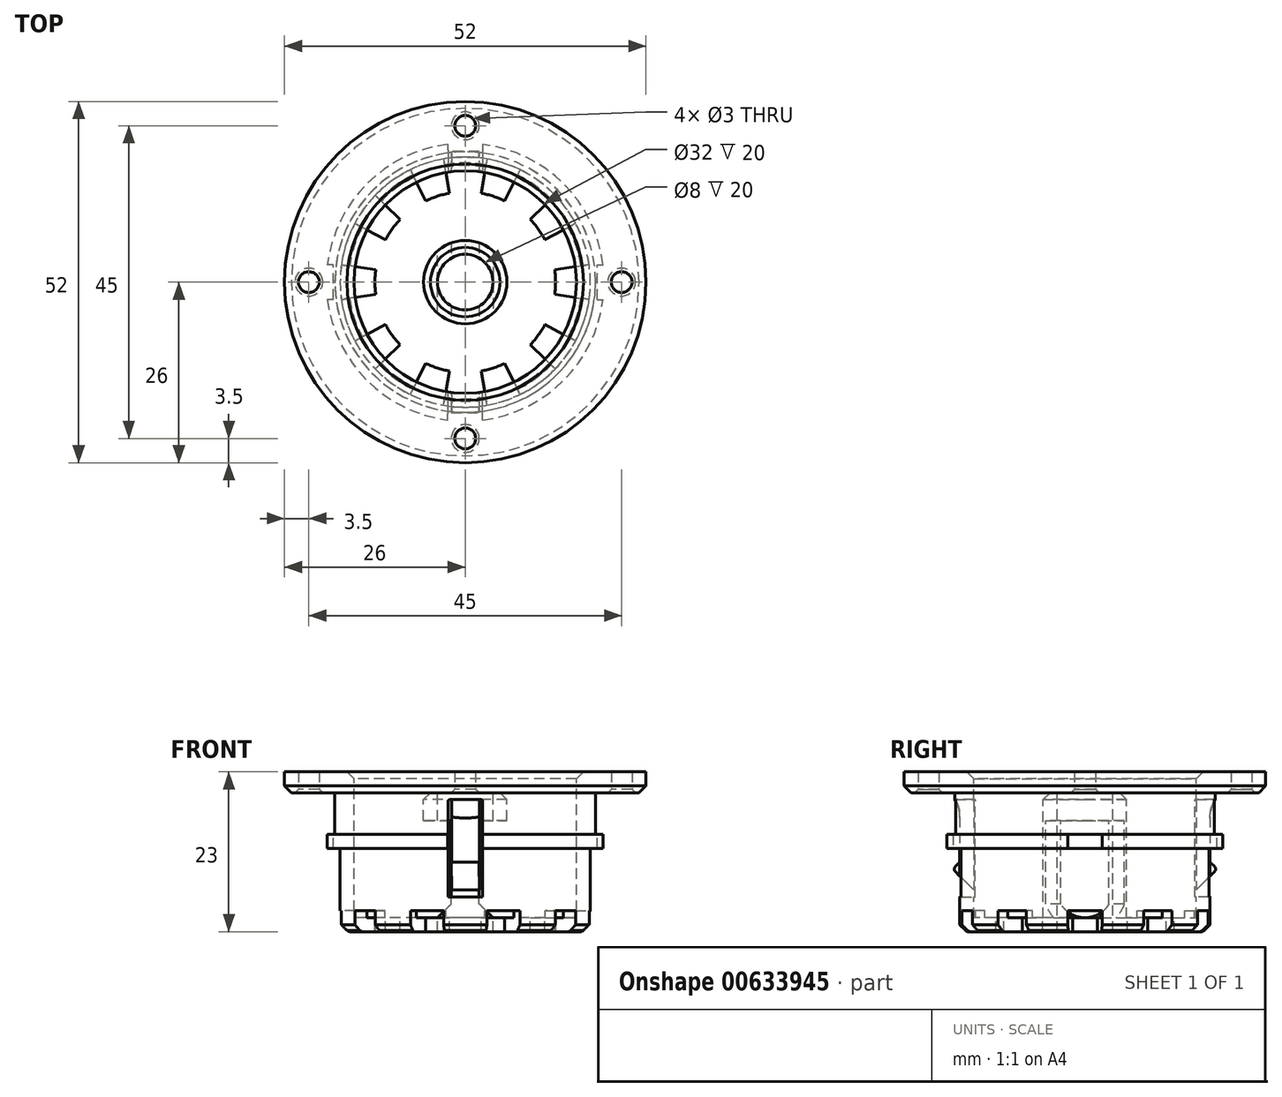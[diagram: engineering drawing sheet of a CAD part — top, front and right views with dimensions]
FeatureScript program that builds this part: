
annotation { "Feature Type Name" : "Feature", "Feature Type Description" : "" }
export const myFeature = defineFeature(function(context is Context, id is Id, definition is map)
    precondition{}
    {
        {
            var Q0;
            Q0=qCreatedBy(makeId("Top.planeOp"),FACE);
            var sketch = newSketch(context, id + "F0", { "sketchPlane" : qUnion([Q0])});
            skCircle(sketch, "E0", {"center": v(0, 0) * mm, "radius": 18 * mm});
            skSolve(sketch);
        }
        {
            var Q0;
            Q0=qCreatedBy(makeId("Top.planeOp"),FACE);
            var sketch = newSketch(context, id + "F1", { "sketchPlane" : qUnion([Q0])});
            skCircle(sketch, "E1", {"center": v(0, 0) * mm, "radius": 18.75 * mm});
            skSolve(sketch);
        }
        {
            var Q0;
            Q0=qCreatedBy(makeId("Top.planeOp"),FACE);
            var sketch = newSketch(context, id + "F2", { "sketchPlane" : qUnion([Q0])});
            skCircle(sketch, "E2", {"center": v(0, 0) * mm, "radius": 20 * mm});
            skLineSegment(sketch, "E3.bottom", {"start": v(19, -2.5) * mm, "end": v(21, -2.5) * mm});
            skLineSegment(sketch, "E3.top", {"start": v(19, 2.5) * mm, "end": v(21, 2.5) * mm});
            skLineSegment(sketch, "E3.left", {"start": v(19, -2.5) * mm, "end": v(19, 2.5) * mm});
            skLineSegment(sketch, "E3.right", {"start": v(21, -2.5) * mm, "end": v(21, 2.5) * mm});
            skPoint(sketch, "E3.middle", {"position": v(20, 0) * mm});
            skLineSegment(sketch, "E4.MirrorCS", {"start": v(-19, -2.5) * mm, "end": v(-21, -2.5) * mm});
            skLineSegment(sketch, "E5.MirrorCS", {"start": v(-21, -2.5) * mm, "end": v(-21, 2.5) * mm});
            skLineSegment(sketch, "E6.MirrorCS", {"start": v(-19, -2.5) * mm, "end": v(-19, 2.5) * mm});
            skLineSegment(sketch, "E7.MirrorCS", {"start": v(-19, 2.5) * mm, "end": v(-21, 2.5) * mm});
            skPoint(sketch, "E8.MirrorP", {"position": v(-20, 0) * mm});
            skLineSegment(sketch, "E9.bottom", {"start": v(2.5, -19) * mm, "end": v(-2.5, -19) * mm});
            skLineSegment(sketch, "E9.top", {"start": v(2.5, -21) * mm, "end": v(-2.5, -21) * mm});
            skLineSegment(sketch, "E9.left", {"start": v(2.5, -21) * mm, "end": v(2.5, -19) * mm});
            skLineSegment(sketch, "E9.right", {"start": v(-2.5, -21) * mm, "end": v(-2.5, -19) * mm});
            skPoint(sketch, "E9.middle", {"position": v(0, -20) * mm});
            skLineSegment(sketch, "E10.MirrorCS", {"start": v(2.5, 21) * mm, "end": v(2.5, 19) * mm});
            skLineSegment(sketch, "E11.MirrorCS", {"start": v(2.5, 21) * mm, "end": v(-2.5, 21) * mm});
            skLineSegment(sketch, "E12.MirrorCS", {"start": v(2.5, 19) * mm, "end": v(-2.5, 19) * mm});
            skLineSegment(sketch, "E13.MirrorCS", {"start": v(-2.5, 21) * mm, "end": v(-2.5, 19) * mm});
            skSolve(sketch);
        }
        {
            var Q0;
            Q0 = qSketchRegion(id + "F0", true);
            extrude(context, id + "F3", {"entities" : qUnion([Q0]), "oppositeDirection" : true, "depth" : 20 * mm, "offsetDistance" : 25 * mm});
        }
        {
            var Q0;
            Q0 = qSketchRegion(id + "F1", true);
            extrude(context, id + "F4", {"entities" : qUnion([Q0]), "operationType" : NewBodyOperationType.ADD, "oppositeDirection" : true, "depth" : 6 * mm, "offsetDistance" : 25 * mm});
        }
        {
            var Q0;
            {var subQ13=sQuery(id+"F2.wireOp",EDGE,"E3.left");Q0=makeQuery(id+"F2.imprint","IMPRINT",FACE,{"disambiguationData":[TD([[makeQuery(id+"F2.imprint","IMPRINT",EDGE,{"derivedFrom":subQ13}),1.0]])]});}
            extrude(context, id + "F5", {"entities" : qUnion([Q0]), "operationType" : NewBodyOperationType.ADD, "oppositeDirection" : true, "depth" : 8 * mm, "offsetDistance" : 25 * mm, "hasSecondDirection" : true, "secondDirectionOppositeDirection" : true, "secondDirectionDepth" : 6 * mm});
        }
        {
            var Q0;
            Q0=qCreatedBy(makeId("Top.planeOp"),FACE);
            var sketch = newSketch(context, id + "F6", { "sketchPlane" : qUnion([Q0])});
            skCircle(sketch, "E14", {"center": v(0, 0) * mm, "radius": 4 * mm});
            skSolve(sketch);
        }
        {
            var Q0;
            Q0 = qSketchRegion(id + "F6", true);
            extrude(context, id + "F7", {"entities" : qUnion([Q0]), "operationType" : NewBodyOperationType.REMOVE, "oppositeDirection" : true, "depth" : 20 * mm, "offsetDistance" : 25 * mm});
        }
        {
            var Q0;
            Q0=qCreatedBy(makeId("Top.planeOp"),FACE);
            var sketch = newSketch(context, id + "F8", { "sketchPlane" : qUnion([Q0])});
            skCircle(sketch, "E15", {"center": v(0, 0) * mm, "radius": 16 * mm});
            skCircle(sketch, "E16", {"center": v(0, 0) * mm, "radius": 6 * mm});
            skSolve(sketch);
        }
        {
            var Q0;
            Q0 = qSketchRegion(id + "F8", true);
            extrude(context, id + "F9", {"entities" : qUnion([Q0]), "operationType" : NewBodyOperationType.REMOVE, "oppositeDirection" : true, "depth" : 18 * mm, "offsetDistance" : 25 * mm});
        }
        {
            var Q0;
            Q0=qCreatedBy(makeId("Top.planeOp"),FACE);
            var sketch = newSketch(context, id + "F10", { "sketchPlane" : qUnion([Q0])});
            skLineSegment(sketch, "E17.bottom", {"start": v(6, 6) * mm, "end": v(2, 6) * mm});
            skLineSegment(sketch, "E17.top", {"start": v(6, -6) * mm, "end": v(2, -6) * mm});
            skLineSegment(sketch, "E17.left", {"start": v(6, 6) * mm, "end": v(6, -6) * mm});
            skLineSegment(sketch, "E17.right", {"start": v(2, 6) * mm, "end": v(2, -6) * mm});
            skPoint(sketch, "E17.middle", {"position": v(4, 0) * mm});
            skPoint(sketch, "E18.MirrorP", {"position": v(-4, 0) * mm});
            skLineSegment(sketch, "E19.MirrorCS", {"start": v(-6, 6) * mm, "end": v(-2, 6) * mm});
            skLineSegment(sketch, "E20.MirrorCS", {"start": v(-6, 6) * mm, "end": v(-6, -6) * mm});
            skLineSegment(sketch, "E21.MirrorCS", {"start": v(-6, -6) * mm, "end": v(-2, -6) * mm});
            skLineSegment(sketch, "E22.MirrorCS", {"start": v(-2, 6) * mm, "end": v(-2, -6) * mm});
            skSolve(sketch);
        }
        {
            var Q0;
            Q0 = qSketchRegion(id + "F10", true);
            extrude(context, id + "F11", {"entities" : qUnion([Q0]), "operationType" : NewBodyOperationType.REMOVE, "oppositeDirection" : true, "depth" : 18 * mm, "offsetDistance" : 25 * mm, "hasSecondDirection" : true, "secondDirectionOppositeDirection" : true, "secondDirectionDepth" : 4 * mm});
        }
        {
            var Q0;
            Q0=qCreatedBy(makeId("Top.planeOp"),FACE);
            var sketch = newSketch(context, id + "F12", { "sketchPlane" : qUnion([Q0])});
            skCircle(sketch, "E23", {"center": v(0, 0) * mm, "radius": 16 * mm});
            skCircle(sketch, "E24", {"center": v(0, 0) * mm, "radius": 26 * mm});
            skCircle(sketch, "E25", {"center": v(0, 22.5) * mm, "radius": 1.5 * mm});
            skCircle(sketch, "E26.MirrorC", {"center": v(0, -22.5) * mm, "radius": 1.5 * mm});
            skCircle(sketch, "E27", {"center": v(-22.5, 0) * mm, "radius": 1.5 * mm});
            skCircle(sketch, "E28.MirrorC", {"center": v(22.5, 0) * mm, "radius": 1.5 * mm});
            skSolve(sketch);
        }
        {
            var Q0;
            Q0 = qSketchRegion(id + "F12", true);
            extrude(context, id + "F13", {"entities" : qUnion([Q0]), "operationType" : NewBodyOperationType.ADD, "depth" : 3 * mm, "offsetDistance" : 25 * mm});
        }
        {
            var Q0;
            Q0=makeQuery(id+"F11.boolean.opBoolean","COPY",EDGE,{"disambiguationData":[OD(1.0)],"derivedFrom":makeQuery(id+"F11.opExtrude","CAP_EDGE",EDGE,{"disambiguationData":[OSD([sQuery(id+"F10.wireOp",EDGE,"E17.right")])],"isStart":false})});
            var Q1;
            Q1=makeQuery(id+"F11.boolean.opBoolean","COPY",EDGE,{"disambiguationData":[OD(1.0)],"derivedFrom":makeQuery(id+"F11.opExtrude","CAP_EDGE",EDGE,{"disambiguationData":[OSD([sQuery(id+"F10.wireOp",EDGE,"E22.MirrorCS")])],"isStart":false})});
            var Q2;
            Q2=makeQuery(id+"F11.boolean.opBoolean","COPY",EDGE,{"disambiguationData":[OD(0.0)],"derivedFrom":makeQuery(id+"F11.opExtrude","CAP_EDGE",EDGE,{"disambiguationData":[OSD([sQuery(id+"F10.wireOp",EDGE,"E22.MirrorCS")])],"isStart":false})});
            var Q3;
            Q3=makeQuery(id+"F11.boolean.opBoolean","COPY",EDGE,{"disambiguationData":[OD(0.0)],"derivedFrom":makeQuery(id+"F11.opExtrude","CAP_EDGE",EDGE,{"disambiguationData":[OSD([sQuery(id+"F10.wireOp",EDGE,"E17.right")])],"isStart":false})});
            chamfer(context, id + "F14", {"entities" : qUnion([Q0, Q1, Q2, Q3]), "width" : 2 * mm, "tangentPropagation" : true});
        }
        {
            var Q0;
            Q0=makeQuery(id+"F13.opExtrude","CAP_EDGE",EDGE,{"disambiguationData":[OSD([sQuery(id+"F12.wireOp",EDGE,"E23")])],"isStart":false});
            chamfer(context, id + "F15", {"entities" : qUnion([Q0]), "width" : 1 * mm, "tangentPropagation" : true});
        }
        {
            var Q0;
            Q0=makeQuery(id+"F13.opExtrude","CAP_EDGE",EDGE,{"disambiguationData":[OSD([sQuery(id+"F12.wireOp",EDGE,"E26.MirrorC")])],"isStart":true});
            var Q1;
            Q1=makeQuery(id+"F13.opExtrude","CAP_EDGE",EDGE,{"disambiguationData":[OSD([sQuery(id+"F12.wireOp",EDGE,"E28.MirrorC")])],"isStart":true});
            var Q2;
            Q2=makeQuery(id+"F13.opExtrude","CAP_EDGE",EDGE,{"disambiguationData":[OSD([sQuery(id+"F12.wireOp",EDGE,"E25")])],"isStart":true});
            var Q3;
            Q3=makeQuery(id+"F13.opExtrude","CAP_EDGE",EDGE,{"disambiguationData":[OSD([sQuery(id+"F12.wireOp",EDGE,"E27")])],"isStart":true});
            chamfer(context, id + "F16", {"entities" : qUnion([Q0, Q1, Q2, Q3]), "width" : 0.5 * mm, "tangentPropagation" : true});
        }
        {
            var Q0;
            Q0=makeQuery(id+"F3.opExtrude","CAP_EDGE",EDGE,{"disambiguationData":[OSD([sQuery(id+"F0.wireOp",EDGE,"E0")])],"isStart":false});
            var Q1;
            Q1=makeQuery(id+"F13.opExtrude","CAP_EDGE",EDGE,{"disambiguationData":[OSD([sQuery(id+"F12.wireOp",EDGE,"E24")])],"isStart":true});
            var Q2;
            Q2=makeQuery(id+"F7.boolean.opBoolean","COPY",EDGE,{"derivedFrom":makeQuery(id+"F7.opExtrude","CAP_EDGE",EDGE,{"disambiguationData":[OSD([sQuery(id+"F6.wireOp",EDGE,"E14")])],"isStart":false})});
            var Q3;
            Q3=makeQuery(id+"F9.boolean.opBoolean","COPY",EDGE,{"derivedFrom":makeQuery(id+"F9.opExtrude","CAP_EDGE",EDGE,{"disambiguationData":[OSD([sQuery(id+"F8.wireOp",EDGE,"E16")])],"isStart":true})});
            chamfer(context, id + "F17", {"entities" : qUnion([Q0, Q1, Q2, Q3]), "width" : 1 * mm, "tangentPropagation" : true});
        }
        {
            var Q0;
            Q0=qCreatedBy(makeId("Top.planeOp"),FACE);
            var sketch = newSketch(context, id + "F18", { "sketchPlane" : qUnion([Q0])});
            skLineSegment(sketch, "E29", {"start": v(12.88, 1.8) * mm, "end": v(17.83, 2.5) * mm});
            skLineSegment(sketch, "E30", {"start": v(12.88, -1.8) * mm, "end": v(17.83, -2.5) * mm});
            skArc(sketch, "E31", {"start": v(12.88, -1.8) * mm, "mid": v(13, 0) * mm, "end": v(12.88, 1.8) * mm});
            skArc(sketch, "E32", {"start": v(17.83, -2.5) * mm, "mid": v(18, 0) * mm, "end": v(17.83, 2.5) * mm});
            skArc(sketch, "E33.1.0", {"start": v(11.47, 6.11) * mm, "mid": v(10.52, 7.64) * mm, "end": v(9.36, 9.02) * mm});
            skLineSegment(sketch, "E33.1.1", {"start": v(11.47, 6.11) * mm, "end": v(15.9, 8.46) * mm});
            skArc(sketch, "E33.1.2", {"start": v(15.9, 8.46) * mm, "mid": v(14.56, 10.58) * mm, "end": v(12.95, 12.5) * mm});
            skLineSegment(sketch, "E33.1.3", {"start": v(9.36, 9.02) * mm, "end": v(12.95, 12.5) * mm});
            skArc(sketch, "E33.2.0", {"start": v(5.69, 11.69) * mm, "mid": v(4.02, 12.36) * mm, "end": v(2.27, 12.8) * mm});
            skLineSegment(sketch, "E33.2.1", {"start": v(5.69, 11.69) * mm, "end": v(7.89, 16.18) * mm});
            skArc(sketch, "E33.2.2", {"start": v(7.89, 16.18) * mm, "mid": v(5.56, 17.12) * mm, "end": v(3.13, 17.73) * mm});
            skLineSegment(sketch, "E33.2.3", {"start": v(2.27, 12.8) * mm, "end": v(3.13, 17.73) * mm});
            skArc(sketch, "E33.3.0", {"start": v(-2.27, 12.8) * mm, "mid": v(-4.02, 12.36) * mm, "end": v(-5.69, 11.69) * mm});
            skLineSegment(sketch, "E33.3.1", {"start": v(-2.27, 12.8) * mm, "end": v(-3.13, 17.73) * mm});
            skArc(sketch, "E33.3.2", {"start": v(-3.13, 17.73) * mm, "mid": v(-5.56, 17.12) * mm, "end": v(-7.89, 16.18) * mm});
            skLineSegment(sketch, "E33.3.3", {"start": v(-5.69, 11.69) * mm, "end": v(-7.89, 16.18) * mm});
            skArc(sketch, "E33.4.0", {"start": v(-9.36, 9.02) * mm, "mid": v(-10.52, 7.64) * mm, "end": v(-11.47, 6.11) * mm});
            skLineSegment(sketch, "E33.4.1", {"start": v(-9.36, 9.02) * mm, "end": v(-12.95, 12.5) * mm});
            skArc(sketch, "E33.4.2", {"start": v(-12.95, 12.5) * mm, "mid": v(-14.56, 10.58) * mm, "end": v(-15.9, 8.46) * mm});
            skLineSegment(sketch, "E33.4.3", {"start": v(-11.47, 6.11) * mm, "end": v(-15.9, 8.46) * mm});
            skArc(sketch, "E33.5.0", {"start": v(-12.88, 1.8) * mm, "mid": v(-13, 0) * mm, "end": v(-12.88, -1.8) * mm});
            skLineSegment(sketch, "E33.5.1", {"start": v(-12.88, 1.8) * mm, "end": v(-17.83, 2.5) * mm});
            skArc(sketch, "E33.5.2", {"start": v(-17.83, 2.5) * mm, "mid": v(-18, 0) * mm, "end": v(-17.83, -2.5) * mm});
            skLineSegment(sketch, "E33.5.3", {"start": v(-12.88, -1.8) * mm, "end": v(-17.83, -2.5) * mm});
            skArc(sketch, "E33.6.0", {"start": v(-11.47, -6.11) * mm, "mid": v(-10.52, -7.64) * mm, "end": v(-9.36, -9.02) * mm});
            skLineSegment(sketch, "E33.6.1", {"start": v(-11.47, -6.11) * mm, "end": v(-15.9, -8.46) * mm});
            skArc(sketch, "E33.6.2", {"start": v(-15.9, -8.46) * mm, "mid": v(-14.56, -10.58) * mm, "end": v(-12.95, -12.5) * mm});
            skLineSegment(sketch, "E33.6.3", {"start": v(-9.36, -9.02) * mm, "end": v(-12.95, -12.5) * mm});
            skArc(sketch, "E33.7.0", {"start": v(-5.69, -11.69) * mm, "mid": v(-4.02, -12.36) * mm, "end": v(-2.27, -12.8) * mm});
            skLineSegment(sketch, "E33.7.1", {"start": v(-5.69, -11.69) * mm, "end": v(-7.89, -16.18) * mm});
            skArc(sketch, "E33.7.2", {"start": v(-7.89, -16.18) * mm, "mid": v(-5.56, -17.12) * mm, "end": v(-3.13, -17.73) * mm});
            skLineSegment(sketch, "E33.7.3", {"start": v(-2.27, -12.8) * mm, "end": v(-3.13, -17.73) * mm});
            skArc(sketch, "E33.8.0", {"start": v(2.27, -12.8) * mm, "mid": v(4.02, -12.36) * mm, "end": v(5.69, -11.69) * mm});
            skLineSegment(sketch, "E33.8.1", {"start": v(2.27, -12.8) * mm, "end": v(3.13, -17.73) * mm});
            skArc(sketch, "E33.8.2", {"start": v(3.13, -17.73) * mm, "mid": v(5.56, -17.12) * mm, "end": v(7.89, -16.18) * mm});
            skLineSegment(sketch, "E33.8.3", {"start": v(5.69, -11.69) * mm, "end": v(7.89, -16.18) * mm});
            skArc(sketch, "E33.9.0", {"start": v(9.36, -9.02) * mm, "mid": v(10.52, -7.64) * mm, "end": v(11.47, -6.11) * mm});
            skLineSegment(sketch, "E33.9.1", {"start": v(9.36, -9.02) * mm, "end": v(12.95, -12.5) * mm});
            skArc(sketch, "E33.9.2", {"start": v(12.95, -12.5) * mm, "mid": v(14.56, -10.58) * mm, "end": v(15.9, -8.46) * mm});
            skLineSegment(sketch, "E33.9.3", {"start": v(11.47, -6.11) * mm, "end": v(15.9, -8.46) * mm});
            skPoint(sketch, "E34", {"position": v(18, 0) * mm});
            skSolve(sketch);
        }
        {
            var Q0;
            Q0 = qSketchRegion(id + "F18", true);
            extrude(context, id + "F19", {"entities" : qUnion([Q0]), "operationType" : NewBodyOperationType.REMOVE, "oppositeDirection" : true, "depth" : 25 * mm, "offsetDistance" : 25 * mm, "hasSecondDirection" : true, "secondDirectionOppositeDirection" : true, "secondDirectionDepth" : 17 * mm});
        }
        {
            var Q0;
            Q0=qCreatedBy(makeId("Front.planeOp"),FACE);
            var sketch = newSketch(context, id + "F20", { "sketchPlane" : qUnion([Q0])});
            skLineSegment(sketch, "E35.bottom", {"start": v(-2.48, -1) * mm, "end": v(2.52, -1) * mm});
            skLineSegment(sketch, "E35.top", {"start": v(-2.48, -15) * mm, "end": v(2.52, -15) * mm});
            skLineSegment(sketch, "E35.left", {"start": v(-2.48, -1) * mm, "end": v(-2.48, -15) * mm});
            skLineSegment(sketch, "E35.right", {"start": v(2.52, -1) * mm, "end": v(2.52, -15) * mm});
            skSolve(sketch);
        }
        {
            var Q0;
            Q0 = qSketchRegion(id + "F20", true);
            extrude(context, id + "F21", {"entities" : qUnion([Q0]), "operationType" : NewBodyOperationType.REMOVE, "depth" : 20 * mm, "offsetDistance" : 25 * mm, "hasSecondDirection" : true, "secondDirectionOppositeDirection" : false, "secondDirectionDepth" : 14 * mm});
        }
        {
            var Q0;
            Q0 = qSketchRegion(id + "F20", true);
            extrude(context, id + "F22", {"entities" : qUnion([Q0]), "operationType" : NewBodyOperationType.REMOVE, "oppositeDirection" : true, "depth" : 25 * mm, "offsetDistance" : 25 * mm, "hasSecondDirection" : true, "secondDirectionOppositeDirection" : true, "secondDirectionDepth" : 15 * mm});
        }
        {
            var Q0;
            Q0=qCreatedBy(makeId("Front.planeOp"),FACE);
            var sketch = newSketch(context, id + "F23", { "sketchPlane" : qUnion([Q0])});
            skLineSegment(sketch, "E36.bottom", {"start": v(-1.98, 0) * mm, "end": v(2.02, 0) * mm});
            skLineSegment(sketch, "E36.top", {"start": v(-1.98, -14) * mm, "end": v(2.02, -14) * mm});
            skLineSegment(sketch, "E36.left", {"start": v(-1.98, 0) * mm, "end": v(-1.98, -14) * mm});
            skLineSegment(sketch, "E36.right", {"start": v(2.02, 0) * mm, "end": v(2.02, -14) * mm});
            skSolve(sketch);
        }
        {
            var Q0;
            Q0 = qSketchRegion(id + "F23", true);
            extrude(context, id + "F24", {"entities" : qUnion([Q0]), "operationType" : NewBodyOperationType.ADD, "depth" : 18 * mm, "offsetDistance" : 25 * mm, "hasSecondDirection" : true, "secondDirectionOppositeDirection" : false, "secondDirectionDepth" : 16 * mm});
        }
        {
            var Q0;
            Q0 = qSketchRegion(id + "F23", true);
            extrude(context, id + "F25", {"entities" : qUnion([Q0]), "operationType" : NewBodyOperationType.ADD, "oppositeDirection" : true, "depth" : 18 * mm, "offsetDistance" : 25 * mm, "hasSecondDirection" : true, "secondDirectionOppositeDirection" : true, "secondDirectionDepth" : 16 * mm});
        }
        {
            var Q0;
            Q0=makeQuery(id+"F25.boolean.opBoolean","INTERSECT",EDGE,{"derivedFrom":[makeQuery(id+"F22.boolean.opBoolean","COPY",FACE,{"derivedFrom":makeQuery(id+"F22.opExtrude","SWEPT_FACE",FACE,{"disambiguationData":[OSD([sQuery(id+"F20.wireOp",EDGE,"E35.bottom")])]})}),makeQuery(id+"F25.opExtrude","CAP_FACE",FACE,{"disambiguationData":[OSD([sQuery(id+"F23.wireOp",EDGE,"E36.bottom"),sQuery(id+"F23.wireOp",EDGE,"E36.top"),sQuery(id+"F23.wireOp",EDGE,"E36.left"),sQuery(id+"F23.wireOp",EDGE,"E36.right")])],"isStart":false})]});
            var Q1;
            Q1=makeQuery(id+"F24.boolean.opBoolean","INTERSECT",EDGE,{"derivedFrom":[makeQuery(id+"F21.boolean.opBoolean","COPY",FACE,{"derivedFrom":makeQuery(id+"F21.opExtrude","SWEPT_FACE",FACE,{"disambiguationData":[OSD([sQuery(id+"F20.wireOp",EDGE,"E35.bottom")])]})}),makeQuery(id+"F24.opExtrude","CAP_FACE",FACE,{"disambiguationData":[OSD([sQuery(id+"F23.wireOp",EDGE,"E36.bottom"),sQuery(id+"F23.wireOp",EDGE,"E36.top"),sQuery(id+"F23.wireOp",EDGE,"E36.left"),sQuery(id+"F23.wireOp",EDGE,"E36.right")])],"isStart":false})]});
            fillet(context, id + "F26", {"entities" : qUnion([Q0, Q1]), "radius" : 5 * mm, "tangentPropagation" : true, "allowEdgeOverflow" : false});
        }
        {
            var Q0;
            Q0=qCreatedBy(makeId("Front.planeOp"),FACE);
            var sketch = newSketch(context, id + "F27", { "sketchPlane" : qUnion([Q0])});
            skLineSegment(sketch, "E37.bottom", {"start": v(-2, -14) * mm, "end": v(2, -14) * mm});
            skLineSegment(sketch, "E37.top", {"start": v(-2, -8) * mm, "end": v(2, -8) * mm});
            skLineSegment(sketch, "E37.left", {"start": v(-2, -14) * mm, "end": v(-2, -8) * mm});
            skLineSegment(sketch, "E37.right", {"start": v(2, -14) * mm, "end": v(2, -8) * mm});
            skSolve(sketch);
        }
        {
            var Q0;
            Q0 = qSketchRegion(id + "F27", true);
            extrude(context, id + "F28", {"entities" : qUnion([Q0]), "operationType" : NewBodyOperationType.ADD, "depth" : 19 * mm, "offsetDistance" : 25 * mm, "hasSecondDirection" : true, "secondDirectionOppositeDirection" : false, "secondDirectionDepth" : 18 * mm});
        }
        {
            var Q0;
            Q0=makeQuery(id+"F28.opExtrude","CAP_EDGE",EDGE,{"disambiguationData":[OSD([sQuery(id+"F27.wireOp",EDGE,"E37.top")])],"isStart":false});
            var Q1;
            Q1=makeQuery(id+"F28.opExtrude","CAP_EDGE",EDGE,{"disambiguationData":[OSD([sQuery(id+"F27.wireOp",EDGE,"E37.bottom")])],"isStart":false});
            chamfer(context, id + "F29", {"entities" : qUnion([Q0, Q1]), "width" : 3 * mm, "tangentPropagation" : true});
        }
        {
            var Q0;
            Q0 = qSketchRegion(id + "F27", true);
            extrude(context, id + "F30", {"entities" : qUnion([Q0]), "operationType" : NewBodyOperationType.ADD, "oppositeDirection" : true, "depth" : 19 * mm, "offsetDistance" : 25 * mm, "hasSecondDirection" : true, "secondDirectionOppositeDirection" : true, "secondDirectionDepth" : 18 * mm});
        }
        {
            var Q0;
            Q0=makeQuery(id+"F30.opExtrude","CAP_EDGE",EDGE,{"disambiguationData":[OSD([sQuery(id+"F27.wireOp",EDGE,"E37.top")])],"isStart":false});
            var Q1;
            Q1=makeQuery(id+"F30.opExtrude","CAP_EDGE",EDGE,{"disambiguationData":[OSD([sQuery(id+"F27.wireOp",EDGE,"E37.bottom")])],"isStart":false});
            chamfer(context, id + "F31", {"entities" : qUnion([Q0, Q1]), "width" : 3 * mm, "tangentPropagation" : true});
        }
        {
            var Q0;
            Q0=makeQuery(id+"F21.boolean.opBoolean","COPY",EDGE,{"derivedFrom":makeQuery(id+"F21.opExtrude","SWEPT_EDGE",EDGE,{"disambiguationData":[OSD([sQuery(id+"F20.wireOp",EDGE,"E35.bottom"),sQuery(id+"F20.wireOp",EDGE,"E35.right")])]})});
            var Q1;
            Q1=makeQuery(id+"F24.boolean.opBoolean","INTERSECT",EDGE,{"derivedFrom":[makeQuery(id+"F21.boolean.opBoolean","COPY",FACE,{"derivedFrom":makeQuery(id+"F21.opExtrude","SWEPT_FACE",FACE,{"disambiguationData":[OSD([sQuery(id+"F20.wireOp",EDGE,"E35.bottom")])]})}),makeQuery(id+"F24.opExtrude","SWEPT_FACE",FACE,{"disambiguationData":[OSD([sQuery(id+"F23.wireOp",EDGE,"E36.right")])]})]});
            var Q2;
            Q2=makeQuery(id+"F21.boolean.opBoolean","COPY",EDGE,{"derivedFrom":makeQuery(id+"F21.opExtrude","SWEPT_EDGE",EDGE,{"disambiguationData":[OSD([sQuery(id+"F20.wireOp",EDGE,"E35.bottom"),sQuery(id+"F20.wireOp",EDGE,"E35.left")])]})});
            var Q3;
            Q3=makeQuery(id+"F24.boolean.opBoolean","INTERSECT",EDGE,{"derivedFrom":[makeQuery(id+"F21.boolean.opBoolean","COPY",FACE,{"derivedFrom":makeQuery(id+"F21.opExtrude","SWEPT_FACE",FACE,{"disambiguationData":[OSD([sQuery(id+"F20.wireOp",EDGE,"E35.bottom")])]})}),makeQuery(id+"F24.opExtrude","SWEPT_FACE",FACE,{"disambiguationData":[OSD([sQuery(id+"F23.wireOp",EDGE,"E36.left")])]})]});
            fillet(context, id + "F32", {"entities" : qUnion([Q0, Q1, Q2, Q3]), "radius" : 0.25 * mm, "tangentPropagation" : true, "allowEdgeOverflow" : false});
        }
        {
            var Q0;
            Q0=makeQuery(id+"F22.boolean.opBoolean","COPY",EDGE,{"derivedFrom":makeQuery(id+"F22.opExtrude","SWEPT_EDGE",EDGE,{"disambiguationData":[OSD([sQuery(id+"F20.wireOp",EDGE,"E35.bottom"),sQuery(id+"F20.wireOp",EDGE,"E35.left")])]})});
            var Q1;
            Q1=makeQuery(id+"F25.boolean.opBoolean","INTERSECT",EDGE,{"derivedFrom":[makeQuery(id+"F22.boolean.opBoolean","COPY",FACE,{"derivedFrom":makeQuery(id+"F22.opExtrude","SWEPT_FACE",FACE,{"disambiguationData":[OSD([sQuery(id+"F20.wireOp",EDGE,"E35.bottom")])]})}),makeQuery(id+"F25.opExtrude","SWEPT_FACE",FACE,{"disambiguationData":[OSD([sQuery(id+"F23.wireOp",EDGE,"E36.right")])]})]});
            var Q2;
            Q2=makeQuery(id+"F25.boolean.opBoolean","INTERSECT",EDGE,{"derivedFrom":[makeQuery(id+"F22.boolean.opBoolean","COPY",FACE,{"derivedFrom":makeQuery(id+"F22.opExtrude","SWEPT_FACE",FACE,{"disambiguationData":[OSD([sQuery(id+"F20.wireOp",EDGE,"E35.bottom")])]})}),makeQuery(id+"F25.opExtrude","SWEPT_FACE",FACE,{"disambiguationData":[OSD([sQuery(id+"F23.wireOp",EDGE,"E36.left")])]})]});
            var Q3;
            Q3=makeQuery(id+"F22.boolean.opBoolean","COPY",EDGE,{"derivedFrom":makeQuery(id+"F22.opExtrude","SWEPT_EDGE",EDGE,{"disambiguationData":[OSD([sQuery(id+"F20.wireOp",EDGE,"E35.bottom"),sQuery(id+"F20.wireOp",EDGE,"E35.right")])]})});
            fillet(context, id + "F33", {"entities" : qUnion([Q0, Q1, Q2, Q3]), "radius" : 0.25 * mm, "tangentPropagation" : true, "allowEdgeOverflow" : false});
        }
        {
            var Q0;
            Q0=makeQuery(id+"F31.opChamfer","BLEND_EDGE",EDGE,{"blendedFrom":[makeQuery(id+"F30.opExtrude","CAP_EDGE",EDGE,{"disambiguationData":[OSD([sQuery(id+"F27.wireOp",EDGE,"E37.bottom")])],"isStart":false}),makeQuery(id+"F30.opExtrude","CAP_EDGE",EDGE,{"disambiguationData":[OSD([sQuery(id+"F27.wireOp",EDGE,"E37.top")])],"isStart":false})],"blendedInto":[]});
            fillet(context, id + "F34", {"entities" : qUnion([Q0]), "radius" : 0.5 * mm, "tangentPropagation" : true, "allowEdgeOverflow" : false});
        }
        {
            var Q0;
            Q0=makeQuery(id+"F29.opChamfer","BLEND_EDGE",EDGE,{"blendedFrom":[makeQuery(id+"F28.opExtrude","CAP_EDGE",EDGE,{"disambiguationData":[OSD([sQuery(id+"F27.wireOp",EDGE,"E37.bottom")])],"isStart":false}),makeQuery(id+"F28.opExtrude","CAP_EDGE",EDGE,{"disambiguationData":[OSD([sQuery(id+"F27.wireOp",EDGE,"E37.top")])],"isStart":false})],"blendedInto":[]});
            fillet(context, id + "F35", {"entities" : qUnion([Q0]), "radius" : 0.5 * mm, "tangentPropagation" : true, "allowEdgeOverflow" : false});
        }
        {
            var Q0;
            {var subQ0=sQuery(id+"F0.wireOp",EDGE,"E0");Q0=makeQuery(id+"F19.boolean.opBoolean","SPLIT",EDGE,{"disambiguationData":[topologyDisambiguationEdgeConnected([makeQuery(id+"F17.opChamfer","BLEND_FACE",FACE,{"disambiguationData":[OSD([subQ0])]}),makeQuery(id+"F19.opExtrude","SWEPT_FACE",FACE,{"disambiguationData":[OSD([sQuery(id+"F18.wireOp",EDGE,"E33.7.2")])]})])],"derivedFrom":makeQuery(id+"F17.opChamfer","BLEND_EDGE",EDGE,{"blendedFrom":[makeQuery(id+"F3.opExtrude","CAP_EDGE",EDGE,{"disambiguationData":[OSD([subQ0])],"isStart":false}),makeQuery(id+"F3.opExtrude","CAP_FACE",FACE,{"disambiguationData":[OSD([subQ0])],"isStart":false})],"blendedInto":[makeQuery(id+"F3.opExtrude","CAP_FACE",FACE,{"disambiguationData":[OSD([subQ0])],"isStart":false})]})});}
            var Q1;
            {var subQ0=sQuery(id+"F0.wireOp",EDGE,"E0");Q1=makeQuery(id+"F19.boolean.opBoolean","SPLIT",EDGE,{"disambiguationData":[topologyDisambiguationEdgeConnected([makeQuery(id+"F17.opChamfer","BLEND_FACE",FACE,{"disambiguationData":[OSD([subQ0])]}),makeQuery(id+"F19.opExtrude","SWEPT_FACE",FACE,{"disambiguationData":[OSD([sQuery(id+"F18.wireOp",EDGE,"E33.8.2")])]})])],"derivedFrom":makeQuery(id+"F17.opChamfer","BLEND_EDGE",EDGE,{"blendedFrom":[makeQuery(id+"F3.opExtrude","CAP_EDGE",EDGE,{"disambiguationData":[OSD([subQ0])],"isStart":false}),makeQuery(id+"F3.opExtrude","CAP_FACE",FACE,{"disambiguationData":[OSD([subQ0])],"isStart":false})],"blendedInto":[makeQuery(id+"F3.opExtrude","CAP_FACE",FACE,{"disambiguationData":[OSD([subQ0])],"isStart":false})]})});}
            var Q2;
            {var subQ0=sQuery(id+"F0.wireOp",EDGE,"E0");Q2=makeQuery(id+"F19.boolean.opBoolean","SPLIT",EDGE,{"disambiguationData":[topologyDisambiguationEdgeConnected([makeQuery(id+"F17.opChamfer","BLEND_FACE",FACE,{"disambiguationData":[OSD([subQ0])]}),makeQuery(id+"F19.opExtrude","SWEPT_FACE",FACE,{"disambiguationData":[OSD([sQuery(id+"F18.wireOp",EDGE,"E33.9.2")])]})])],"derivedFrom":makeQuery(id+"F17.opChamfer","BLEND_EDGE",EDGE,{"blendedFrom":[makeQuery(id+"F3.opExtrude","CAP_EDGE",EDGE,{"disambiguationData":[OSD([subQ0])],"isStart":false}),makeQuery(id+"F3.opExtrude","CAP_FACE",FACE,{"disambiguationData":[OSD([subQ0])],"isStart":false})],"blendedInto":[makeQuery(id+"F3.opExtrude","CAP_FACE",FACE,{"disambiguationData":[OSD([subQ0])],"isStart":false})]})});}
            var Q3;
            {var subQ0=sQuery(id+"F0.wireOp",EDGE,"E0");Q3=makeQuery(id+"F19.boolean.opBoolean","SPLIT",EDGE,{"disambiguationData":[topologyDisambiguationEdgeConnected([makeQuery(id+"F17.opChamfer","BLEND_FACE",FACE,{"disambiguationData":[OSD([subQ0])]}),makeQuery(id+"F19.opExtrude","SWEPT_FACE",FACE,{"disambiguationData":[OSD([sQuery(id+"F18.wireOp",EDGE,"E32")])]})])],"derivedFrom":makeQuery(id+"F17.opChamfer","BLEND_EDGE",EDGE,{"blendedFrom":[makeQuery(id+"F3.opExtrude","CAP_EDGE",EDGE,{"disambiguationData":[OSD([subQ0])],"isStart":false}),makeQuery(id+"F3.opExtrude","CAP_FACE",FACE,{"disambiguationData":[OSD([subQ0])],"isStart":false})],"blendedInto":[makeQuery(id+"F3.opExtrude","CAP_FACE",FACE,{"disambiguationData":[OSD([subQ0])],"isStart":false})]})});}
            var Q4;
            {var subQ0=sQuery(id+"F0.wireOp",EDGE,"E0");Q4=makeQuery(id+"F19.boolean.opBoolean","SPLIT",EDGE,{"disambiguationData":[topologyDisambiguationEdgeConnected([makeQuery(id+"F17.opChamfer","BLEND_FACE",FACE,{"disambiguationData":[OSD([subQ0])]}),makeQuery(id+"F19.opExtrude","SWEPT_FACE",FACE,{"disambiguationData":[OSD([sQuery(id+"F18.wireOp",EDGE,"E33.1.2")])]})])],"derivedFrom":makeQuery(id+"F17.opChamfer","BLEND_EDGE",EDGE,{"blendedFrom":[makeQuery(id+"F3.opExtrude","CAP_EDGE",EDGE,{"disambiguationData":[OSD([subQ0])],"isStart":false}),makeQuery(id+"F3.opExtrude","CAP_FACE",FACE,{"disambiguationData":[OSD([subQ0])],"isStart":false})],"blendedInto":[makeQuery(id+"F3.opExtrude","CAP_FACE",FACE,{"disambiguationData":[OSD([subQ0])],"isStart":false})]})});}
            var Q5;
            {var subQ0=sQuery(id+"F0.wireOp",EDGE,"E0");Q5=makeQuery(id+"F19.boolean.opBoolean","SPLIT",EDGE,{"disambiguationData":[topologyDisambiguationEdgeConnected([makeQuery(id+"F17.opChamfer","BLEND_FACE",FACE,{"disambiguationData":[OSD([subQ0])]}),makeQuery(id+"F19.opExtrude","SWEPT_FACE",FACE,{"disambiguationData":[OSD([sQuery(id+"F18.wireOp",EDGE,"E33.2.2")])]})])],"derivedFrom":makeQuery(id+"F17.opChamfer","BLEND_EDGE",EDGE,{"blendedFrom":[makeQuery(id+"F3.opExtrude","CAP_EDGE",EDGE,{"disambiguationData":[OSD([subQ0])],"isStart":false}),makeQuery(id+"F3.opExtrude","CAP_FACE",FACE,{"disambiguationData":[OSD([subQ0])],"isStart":false})],"blendedInto":[makeQuery(id+"F3.opExtrude","CAP_FACE",FACE,{"disambiguationData":[OSD([subQ0])],"isStart":false})]})});}
            var Q6;
            {var subQ0=sQuery(id+"F0.wireOp",EDGE,"E0");Q6=makeQuery(id+"F19.boolean.opBoolean","SPLIT",EDGE,{"disambiguationData":[topologyDisambiguationEdgeConnected([makeQuery(id+"F17.opChamfer","BLEND_FACE",FACE,{"disambiguationData":[OSD([subQ0])]}),makeQuery(id+"F19.opExtrude","SWEPT_FACE",FACE,{"disambiguationData":[OSD([sQuery(id+"F18.wireOp",EDGE,"E33.3.2")])]})])],"derivedFrom":makeQuery(id+"F17.opChamfer","BLEND_EDGE",EDGE,{"blendedFrom":[makeQuery(id+"F3.opExtrude","CAP_EDGE",EDGE,{"disambiguationData":[OSD([subQ0])],"isStart":false}),makeQuery(id+"F3.opExtrude","CAP_FACE",FACE,{"disambiguationData":[OSD([subQ0])],"isStart":false})],"blendedInto":[makeQuery(id+"F3.opExtrude","CAP_FACE",FACE,{"disambiguationData":[OSD([subQ0])],"isStart":false})]})});}
            var Q7;
            {var subQ0=sQuery(id+"F0.wireOp",EDGE,"E0");Q7=makeQuery(id+"F19.boolean.opBoolean","SPLIT",EDGE,{"disambiguationData":[topologyDisambiguationEdgeConnected([makeQuery(id+"F17.opChamfer","BLEND_FACE",FACE,{"disambiguationData":[OSD([subQ0])]}),makeQuery(id+"F19.opExtrude","SWEPT_FACE",FACE,{"disambiguationData":[OSD([sQuery(id+"F18.wireOp",EDGE,"E33.4.2")])]})])],"derivedFrom":makeQuery(id+"F17.opChamfer","BLEND_EDGE",EDGE,{"blendedFrom":[makeQuery(id+"F3.opExtrude","CAP_EDGE",EDGE,{"disambiguationData":[OSD([subQ0])],"isStart":false}),makeQuery(id+"F3.opExtrude","CAP_FACE",FACE,{"disambiguationData":[OSD([subQ0])],"isStart":false})],"blendedInto":[makeQuery(id+"F3.opExtrude","CAP_FACE",FACE,{"disambiguationData":[OSD([subQ0])],"isStart":false})]})});}
            var Q8;
            {var subQ0=sQuery(id+"F0.wireOp",EDGE,"E0");Q8=makeQuery(id+"F19.boolean.opBoolean","SPLIT",EDGE,{"disambiguationData":[topologyDisambiguationEdgeConnected([makeQuery(id+"F17.opChamfer","BLEND_FACE",FACE,{"disambiguationData":[OSD([subQ0])]}),makeQuery(id+"F19.opExtrude","SWEPT_FACE",FACE,{"disambiguationData":[OSD([sQuery(id+"F18.wireOp",EDGE,"E33.5.2")])]})])],"derivedFrom":makeQuery(id+"F17.opChamfer","BLEND_EDGE",EDGE,{"blendedFrom":[makeQuery(id+"F3.opExtrude","CAP_EDGE",EDGE,{"disambiguationData":[OSD([subQ0])],"isStart":false}),makeQuery(id+"F3.opExtrude","CAP_FACE",FACE,{"disambiguationData":[OSD([subQ0])],"isStart":false})],"blendedInto":[makeQuery(id+"F3.opExtrude","CAP_FACE",FACE,{"disambiguationData":[OSD([subQ0])],"isStart":false})]})});}
            var Q9;
            {var subQ0=sQuery(id+"F0.wireOp",EDGE,"E0");Q9=makeQuery(id+"F19.boolean.opBoolean","SPLIT",EDGE,{"disambiguationData":[topologyDisambiguationEdgeConnected([makeQuery(id+"F17.opChamfer","BLEND_FACE",FACE,{"disambiguationData":[OSD([subQ0])]}),makeQuery(id+"F19.opExtrude","SWEPT_FACE",FACE,{"disambiguationData":[OSD([sQuery(id+"F18.wireOp",EDGE,"E33.6.2")])]})])],"derivedFrom":makeQuery(id+"F17.opChamfer","BLEND_EDGE",EDGE,{"blendedFrom":[makeQuery(id+"F3.opExtrude","CAP_EDGE",EDGE,{"disambiguationData":[OSD([subQ0])],"isStart":false}),makeQuery(id+"F3.opExtrude","CAP_FACE",FACE,{"disambiguationData":[OSD([subQ0])],"isStart":false})],"blendedInto":[makeQuery(id+"F3.opExtrude","CAP_FACE",FACE,{"disambiguationData":[OSD([subQ0])],"isStart":false})]})});}
            chamfer(context, id + "F36", {"entities" : qUnion([Q0, Q1, Q2, Q3, Q4, Q5, Q6, Q7, Q8, Q9]), "width" : 0.5 * mm, "tangentPropagation" : true});
        }
    });
